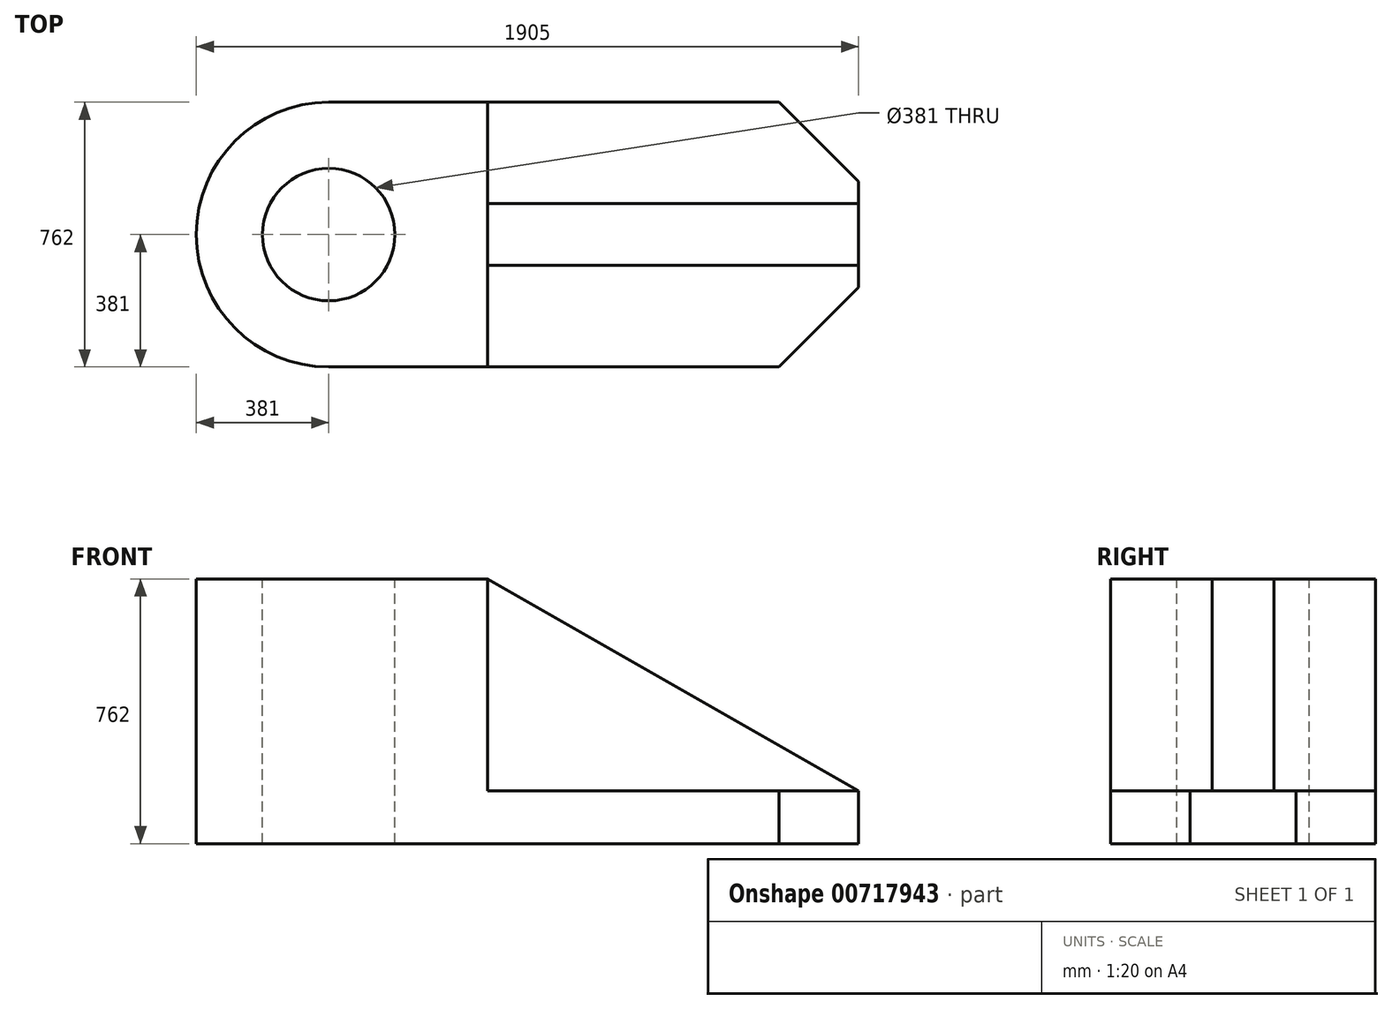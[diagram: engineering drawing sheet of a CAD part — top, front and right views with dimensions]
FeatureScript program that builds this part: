
annotation { "Feature Type Name" : "Feature", "Feature Type Description" : "" }
export const myFeature = defineFeature(function(context is Context, id is Id, definition is map)
    precondition{}
    {
        {
            var Q0;
            Q0=qCreatedBy(makeId("Top.planeOp"),FACE);
            var sketch = newSketch(context, id + "F0", { "sketchPlane" : qUnion([Q0])});
            skLineSegment(sketch, "E0.bottom", {"start": v(762, 381) * mm, "end": v(-762, 381) * mm});
            skLineSegment(sketch, "E0.top", {"start": v(762, -381) * mm, "end": v(-762, -381) * mm});
            skLineSegment(sketch, "E0.left", {"start": v(762, 381) * mm, "end": v(762, -381) * mm});
            skLineSegment(sketch, "E0.right", {"start": v(-762, 381) * mm, "end": v(-762, -381) * mm});
            skPoint(sketch, "E0.middle", {"position": v(0, 0) * mm});
            skArc(sketch, "E1", {"start": v(-762, 381) * mm, "mid": v(-1143, 0) * mm, "end": v(-762, -381) * mm});
            skSolve(sketch);
        }
        {
            var Q0;
            Q0=makeQuery(id+"F0.imprint","IMPRINT",FACE,{"disambiguationData":[TD([[makeQuery(id+"F0.imprint","IMPRINT",EDGE,{"derivedFrom":sQuery(id+"F0.wireOp",EDGE,"E0.bottom")}),1.0]])]});
            var Q1;
            Q1=makeQuery(id+"F0.imprint","IMPRINT",FACE,{"disambiguationData":[TD([[makeQuery(id+"F0.imprint","IMPRINT",EDGE,{"derivedFrom":sQuery(id+"F0.wireOp",EDGE,"E0.right")}),-1.0]])]});
            extrude(context, id + "F1", {"entities" : qUnion([Q0, Q1]), "depth" : 152.4 * mm, "offsetDistance" : 25.4 * mm});
        }
        {
            var Q0;
            Q0=makeQuery(id+"F1.opExtrude","CAP_FACE",FACE,{"disambiguationData":[OSD([sQuery(id+"F0.wireOp",EDGE,"E0.bottom"),sQuery(id+"F0.wireOp",EDGE,"E0.top"),sQuery(id+"F0.wireOp",EDGE,"E0.left"),sQuery(id+"F0.wireOp",EDGE,"E1")])],"isStart":false});
            var sketch = newSketch(context, id + "F2", { "sketchPlane" : qUnion([Q0])});
            skArc(sketch, "E2", {"start": v(-762, 381) * mm, "mid": v(-1143, 0) * mm, "end": v(-762, -381) * mm});
            skLineSegment(sketch, "E3.bottom", {"start": v(-762, 381) * mm, "end": v(-304.8, 381) * mm});
            skLineSegment(sketch, "E3.top", {"start": v(-762, -381) * mm, "end": v(-304.8, -381) * mm});
            skLineSegment(sketch, "E3.left", {"start": v(-762, 381) * mm, "end": v(-762, -381) * mm});
            skLineSegment(sketch, "E3.right", {"start": v(-304.8, 381) * mm, "end": v(-304.8, -381) * mm});
            skSolve(sketch);
        }
        {
            var Q0;
            Q0=makeQuery(id+"F2.imprint","IMPRINT",FACE,{"disambiguationData":[TD([[makeQuery(id+"F2.imprint","IMPRINT",EDGE,{"derivedFrom":sQuery(id+"F2.wireOp",EDGE,"E2")}),1.0]])]});
            var Q1;
            Q1=makeQuery(id+"F2.imprint","IMPRINT",FACE,{"disambiguationData":[TD([[makeQuery(id+"F2.imprint","IMPRINT",EDGE,{"derivedFrom":sQuery(id+"F2.wireOp",EDGE,"E3.bottom")}),1.0]])]});
            extrude(context, id + "F3", {"entities" : qUnion([Q0, Q1]), "operationType" : NewBodyOperationType.ADD, "depth" : 609.6 * mm, "offsetDistance" : 25.4 * mm});
        }
        {
            var Q0;
            Q0=qCreatedBy(makeId("Front.planeOp"),FACE);
            var sketch = newSketch(context, id + "F4", { "sketchPlane" : qUnion([Q0])});
            skLineSegment(sketch, "E4", {"start": v(-304.8, 762) * mm, "end": v(762, 152.4) * mm});
            skLineSegment(sketch, "E5", {"start": v(-304.8, 762) * mm, "end": v(-304.8, 152.4) * mm});
            skLineSegment(sketch, "E6", {"start": v(-304.8, 152.4) * mm, "end": v(762, 152.4) * mm});
            skSolve(sketch);
        }
        {
            var Q0;
            Q0=makeQuery(id+"F4.imprint","IMPRINT",FACE,{"disambiguationData":[TD([[makeQuery(id+"F4.imprint","IMPRINT",EDGE,{"derivedFrom":sQuery(id+"F4.wireOp",EDGE,"E4")}),-1.0]])]});
            extrude(context, id + "F5", {"entities" : qUnion([Q0]), "operationType" : NewBodyOperationType.ADD, "endBound" : BoundingType.SYMMETRIC, "depth" : 177.8 * mm, "offsetDistance" : 25.4 * mm});
        }
        {
            var Q0;
            Q0=makeQuery(id+"F3.opExtrude","CAP_FACE",FACE,{"disambiguationData":[OSD([sQuery(id+"F2.wireOp",EDGE,"E2"),sQuery(id+"F2.wireOp",EDGE,"E3.bottom"),sQuery(id+"F2.wireOp",EDGE,"E3.top"),sQuery(id+"F2.wireOp",EDGE,"E3.right")])],"isStart":false});
            var sketch = newSketch(context, id + "F6", { "sketchPlane" : qUnion([Q0])});
            skCircle(sketch, "E7", {"center": v(-762, 0) * mm, "radius": 190.5 * mm});
            skSolve(sketch);
        }
        {
            var Q0;
            Q0=makeQuery(id+"F6.imprint","IMPRINT",FACE,{"disambiguationData":[TD([[makeQuery(id+"F6.imprint","IMPRINT",EDGE,{"derivedFrom":sQuery(id+"F6.wireOp",EDGE,"E7")}),1.0]])]});
            extrude(context, id + "F7", {"entities" : qUnion([Q0]), "operationType" : NewBodyOperationType.REMOVE, "oppositeDirection" : true, "depth" : 1524 * mm, "offsetDistance" : 25.4 * mm});
        }
        {
            var Q0;
            {var subQ1=sQuery(id+"F0.wireOp",EDGE,"E0.left");var subQ2=sQuery(id+"F0.wireOp",EDGE,"E0.bottom");Q0=makeQuery(id+"F5.boolean.opBoolean","SPLIT",FACE,{"disambiguationData":[TD([makeQuery(id+"F1.opExtrude","SWEPT_FACE",FACE,{"disambiguationData":[OSD([subQ2])]})])],"derivedFrom":makeQuery(id+"F1.opExtrude","CAP_FACE",FACE,{"disambiguationData":[OSD([subQ2,sQuery(id+"F0.wireOp",EDGE,"E0.top"),subQ1,sQuery(id+"F0.wireOp",EDGE,"E1")])],"isStart":false})});}
            var sketch = newSketch(context, id + "F8", { "sketchPlane" : qUnion([Q0])});
            skLineSegment(sketch, "E8", {"start": v(762, -152.4) * mm, "end": v(533.4, -381) * mm});
            skLineSegment(sketch, "E9", {"start": v(533.4, -381) * mm, "end": v(762, -381) * mm});
            skLineSegment(sketch, "E10", {"start": v(762, -381) * mm, "end": v(762, -152.4) * mm});
            skLineSegment(sketch, "E11", {"start": v(533.4, 381) * mm, "end": v(762, 152.4) * mm});
            skLineSegment(sketch, "E12", {"start": v(762, 152.4) * mm, "end": v(762, 381) * mm});
            skLineSegment(sketch, "E13", {"start": v(762, 381) * mm, "end": v(533.4, 381) * mm});
            skSolve(sketch);
        }
        {
            var Q0;
            Q0=makeQuery(id+"F8.imprint","IMPRINT",FACE,{"disambiguationData":[TD([[makeQuery(id+"F8.imprint","IMPRINT",EDGE,{"derivedFrom":sQuery(id+"F8.wireOp",EDGE,"E11")}),1.0]])]});
            var Q1;
            Q1=makeQuery(id+"F8.imprint","IMPRINT",FACE,{"disambiguationData":[TD([[makeQuery(id+"F8.imprint","IMPRINT",EDGE,{"derivedFrom":sQuery(id+"F8.wireOp",EDGE,"E8")}),1.0]])]});
            extrude(context, id + "F9", {"entities" : qUnion([Q0, Q1]), "operationType" : NewBodyOperationType.REMOVE, "oppositeDirection" : true, "depth" : 152.4 * mm, "offsetDistance" : 25.4 * mm});
        }
    });
